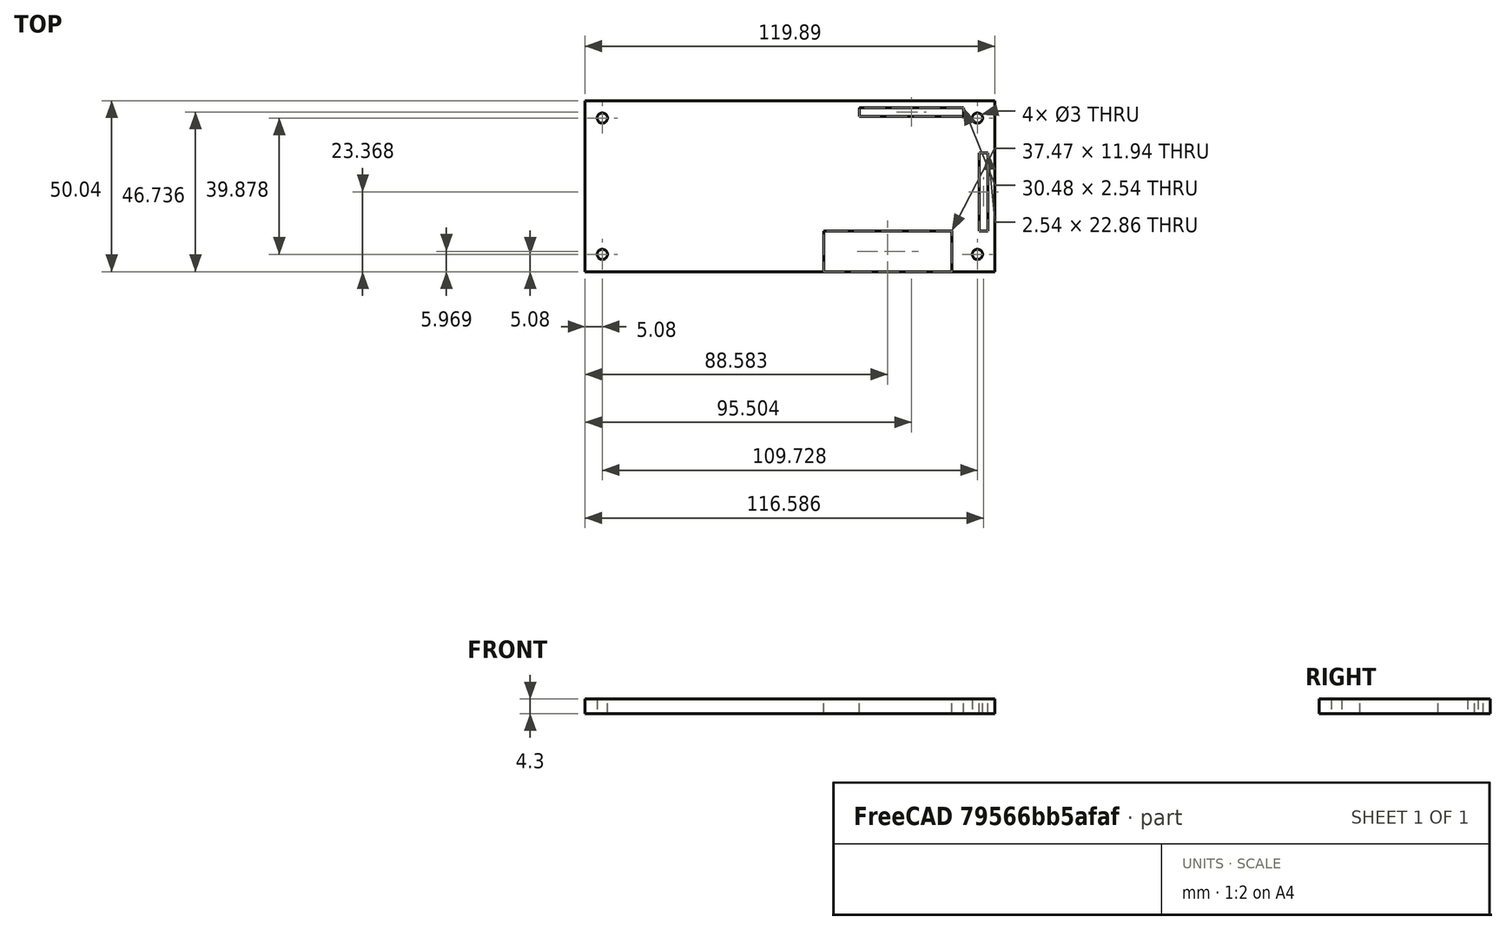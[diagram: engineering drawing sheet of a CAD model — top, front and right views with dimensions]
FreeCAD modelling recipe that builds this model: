
FCSTD DOCUMENT  (FreeCAD 0.20RUnknown)
Label: pn532-breakout
License: All rights reserved
LicenseURL: http://en.wikipedia.org/wiki/All_rights_reserved
objects: Sketcher::SketchObject×1, PartDesign::Pad×1, PartDesign::Body×1
note: 4 computed .brp shape members not serialized (recipe doc carries the construction recipe); baked Part::Feature solids carry a one-line shape summary decoded from their .brp

FEATURE [Sketcher::SketchObject] Sketch
  FullyConstrained = true
  sketch-geometry (30):
    g0: LineSegment StartX=0 StartY=0 StartZ=0 EndX=119.888 EndY=0 EndZ=0
    g1: LineSegment StartX=119.888 StartY=0 StartZ=0 EndX=119.888 EndY=50.038 EndZ=0
    g2: LineSegment StartX=119.888 StartY=50.038 StartZ=0 EndX=0 EndY=50.038 EndZ=0
    g3: LineSegment StartX=0 StartY=50.038 StartZ=0 EndX=0 EndY=0 EndZ=0
    g4: LineSegment StartX=0 StartY=0 StartZ=0 EndX=5.08 EndY=5.08 EndZ=0
    g5: Circle CenterX=5.08 CenterY=5.08 CenterZ=0 NormalX=0 NormalY=0 NormalZ=1 AngleXU=0 Radius=1.5
    g6: LineSegment StartX=0 StartY=50.038 StartZ=0 EndX=5.08 EndY=44.958 EndZ=0
    g7: LineSegment StartX=119.888 StartY=50.038 StartZ=0 EndX=114.808 EndY=44.958 EndZ=0
    g8: LineSegment StartX=119.888 StartY=0 StartZ=0 EndX=114.808 EndY=5.08 EndZ=0
    g9: Circle CenterX=5.08 CenterY=44.958 CenterZ=0 NormalX=0 NormalY=0 NormalZ=1 AngleXU=0 Radius=1.5
    g10: Circle CenterX=114.808 CenterY=44.958 CenterZ=0 NormalX=0 NormalY=0 NormalZ=1 AngleXU=0 Radius=1.5
    g11: Circle CenterX=114.808 CenterY=5.08 CenterZ=0 NormalX=0 NormalY=0 NormalZ=1 AngleXU=0 Radius=1.5
    g12: LineSegment StartX=119.888 StartY=0 StartZ=0 EndX=116.586 EndY=24.638 EndZ=0
    g13: LineSegment StartX=119.888 StartY=50.038 StartZ=0 EndX=95.504 EndY=46.736 EndZ=0
    g14: LineSegment StartX=116.586 StartY=24.638 StartZ=0 EndX=115.316 EndY=34.798 EndZ=0
    g15: LineSegment StartX=95.504 StartY=46.736 StartZ=0 EndX=80.264 EndY=45.466 EndZ=0
    g16: LineSegment StartX=115.316 StartY=34.798 StartZ=0 EndX=117.856 EndY=34.798 EndZ=0
    g17: LineSegment StartX=117.856 StartY=34.798 StartZ=0 EndX=117.856 EndY=11.938 EndZ=0
    g18: LineSegment StartX=117.856 StartY=11.938 StartZ=0 EndX=115.316 EndY=11.938 EndZ=0
    g19: LineSegment StartX=115.316 StartY=11.938 StartZ=0 EndX=115.316 EndY=34.798 EndZ=0
    g20: LineSegment StartX=80.264 StartY=45.466 StartZ=0 EndX=110.744 EndY=45.466 EndZ=0
    g21: LineSegment StartX=110.744 StartY=45.466 StartZ=0 EndX=110.744 EndY=48.006 EndZ=0
    g22: LineSegment StartX=110.744 StartY=48.006 StartZ=0 EndX=80.264 EndY=48.006 EndZ=0
    g23: LineSegment StartX=80.264 StartY=48.006 StartZ=0 EndX=80.264 EndY=45.466 EndZ=0
    g24: LineSegment StartX=115.316 StartY=11.938 StartZ=0 EndX=107.316 EndY=11.938 EndZ=0
    g25: LineSegment StartX=0 StartY=0 StartZ=0 EndX=69.85 EndY=0 EndZ=0
    g26: LineSegment StartX=69.85 StartY=0 StartZ=0 EndX=107.316 EndY=0 EndZ=0
    g27: LineSegment StartX=107.316 StartY=0 StartZ=0 EndX=107.316 EndY=11.938 EndZ=0
    g28: LineSegment StartX=107.316 StartY=11.938 StartZ=0 EndX=69.85 EndY=11.938 EndZ=0
    g29: LineSegment StartX=69.85 StartY=11.938 StartZ=0 EndX=69.85 EndY=0 EndZ=0
  constraints (81):
    c: Coincident(g0,g1)
    c: Coincident(g1,g2)
    c: Coincident(g2,g3)
    c: Coincident(g3,g0)
    c: Horizontal(g0)
    c: Horizontal(g2)
    c: Vertical(g1)
    c: Vertical(g3)
    c: Coincident(g0,g-1)
    c: DistanceY(g3,g3) = 50.038
    c: DistanceX(g0,g0) = 119.888
    c: Coincident(g4,g0)
    c: DistanceX(g4,g4) = 5.08
    c: DistanceY(g4,g4) = 5.08
    c: Coincident(g5,g4)
    c: Diameter(g5) = 3
    c: Coincident(g6,g2)
    c: Coincident(g7,g1)
    c: Coincident(g8,g0)
    c: DistanceY(g7,g7) = 5.08
    c: DistanceY(g8,g8) = 5.08
    c: DistanceY(g6,g6) = 5.08
    c: DistanceX(g7,g7) = 5.08
    c: DistanceX(g8,g8) = 5.08
    c: DistanceX(g6,g6) = 5.08
    c: Coincident(g9,g6)
    c: Coincident(g10,g7)
    c: Coincident(g11,g8)
    c: Diameter(g10) = 3
    c: Diameter(g11) = 3
    c: Diameter(g9) = 3
    c: Coincident(g12,g0)
    c: DistanceX(g12,g12) = 3.302
    c: DistanceY(g12,g12) = 24.638
    c: Coincident(g13,g1)
    c: DistanceX(g13,g13) = 24.384
    c: DistanceY(g13,g13) = 3.302
    c: Coincident(g14,g12)
    c: DistanceY(g14,g14) = 10.16
    c: DistanceX(g14,g14) = 1.27
    c: Coincident(g15,g13)
    c: DistanceX(g15,g15) = 15.24
    c: DistanceY(g15,g15) = 1.27
    c: Coincident(g16,g17)
    c: Coincident(g17,g18)
    c: Coincident(g18,g19)
    c: Coincident(g19,g16)
    c: Horizontal(g16)
    c: Horizontal(g18)
    c: Vertical(g17)
    c: Vertical(g19)
    c: Coincident(g16,g14)
    c: DistanceY(g17,g17) = 22.86
    c: DistanceX(g16,g16) = 2.54
    c: Coincident(g20,g21)
    c: Coincident(g21,g22)
    c: Coincident(g22,g23)
    c: Coincident(g23,g20)
    c: Horizontal(g20)
    c: Horizontal(g22)
    c: Vertical(g21)
    c: Vertical(g23)
    c: Coincident(g20,g15)
    c: DistanceY(g21,g21) = 2.54
    c: DistanceX(g22,g22) = 30.48
    c: Coincident(g24,g18)
    c: Horizontal(g24)
    c: DistanceX(g24,g24) = 8
    c: Coincident(g25,g0)
    c: DistanceX(g25,g25) = 69.85
    c: Horizontal(g25)
    c: Coincident(g26,g27)
    c: Coincident(g27,g28)
    c: Coincident(g28,g29)
    c: Coincident(g29,g26)
    c: Horizontal(g26)
    c: Horizontal(g28)
    c: Vertical(g27)
    c: Vertical(g29)
    c: Coincident(g26,g25)
    c: Coincident(g27,g24)
FEATURE [PartDesign::Pad] Pad
  Direction = (0,0,1)
  Length = 4.3
  Length2 = 10
  Profile = -> Sketch
  ReferenceAxis = -> Sketch [N_Axis]
  Type = 0
FEATURE [PartDesign::Body] Body
  Group = -> [Sketch,Pad]
  Origin = -> Origin
  Tip = -> Pad
